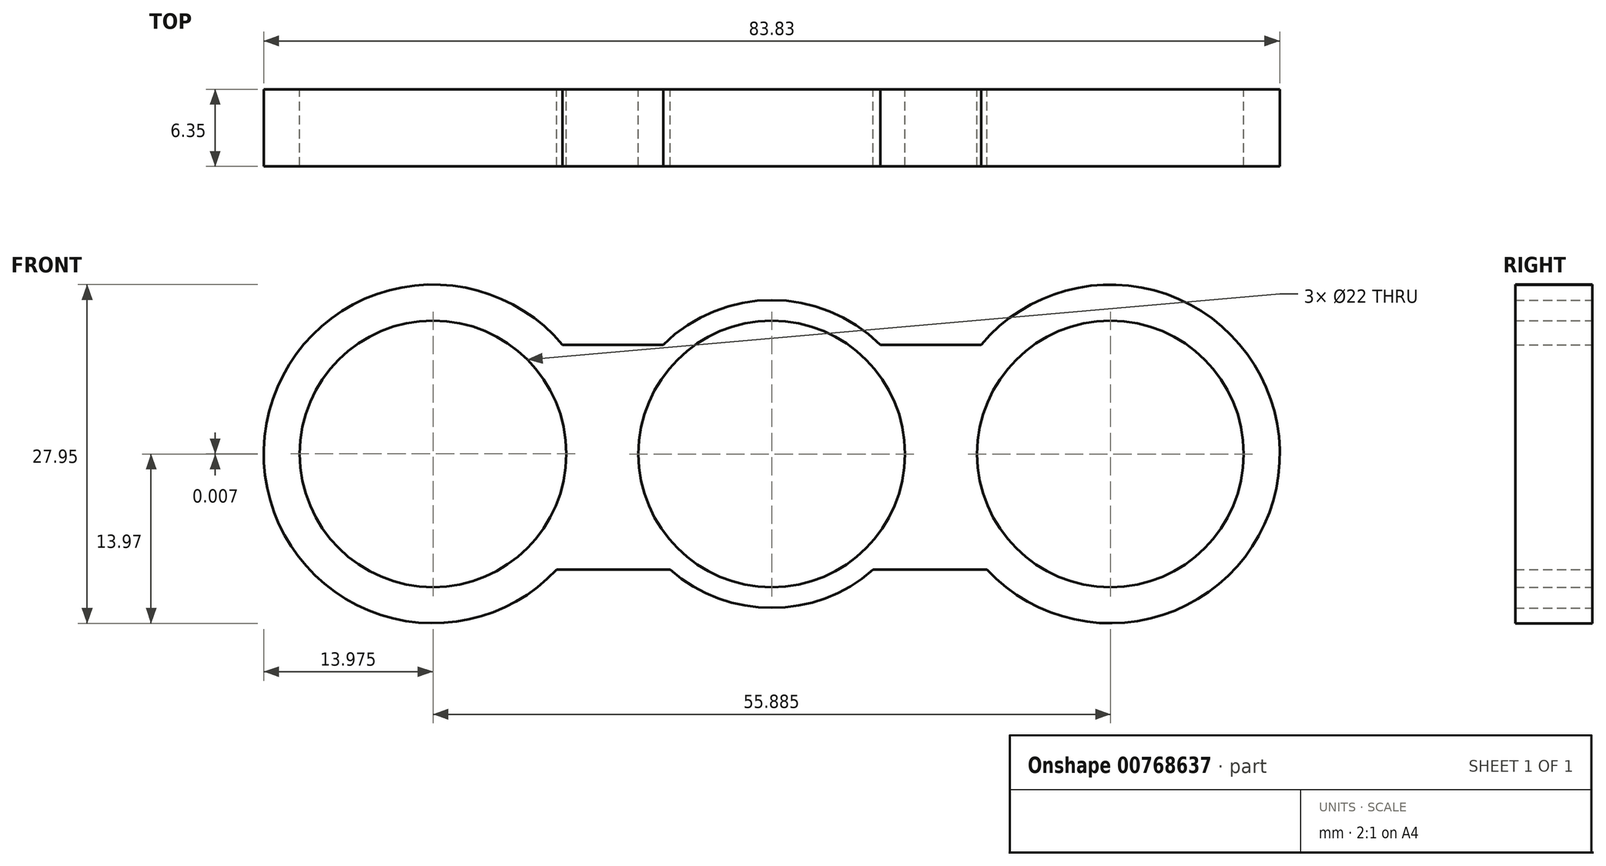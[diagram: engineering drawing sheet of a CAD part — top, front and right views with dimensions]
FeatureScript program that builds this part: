
annotation { "Feature Type Name" : "Feature", "Feature Type Description" : "" }
export const myFeature = defineFeature(function(context is Context, id is Id, definition is map)
    precondition{}
    {
        {
            var Q0;
            Q0=qCreatedBy(makeId("Front.planeOp"),FACE);
            var sketch = newSketch(context, id + "F0", { "sketchPlane" : qUnion([Q0])});
            skCircle(sketch, "E0", {"center": v(0, 0) * mm, "radius": 11 * mm});
            skCircle(sketch, "E1", {"center": v(27.94, 0) * mm, "radius": 11 * mm});
            skCircle(sketch, "E2", {"center": v(-27.95, 0) * mm, "radius": 11 * mm});
            skCircle(sketch, "E3", {"center": v(-27.95, 0) * mm, "radius": 13.97 * mm});
            skCircle(sketch, "E4", {"center": v(27.94, 0) * mm, "radius": 13.97 * mm});
            skCircle(sketch, "E5", {"center": v(0, 0) * mm, "radius": 12.7 * mm});
            skLineSegment(sketch, "E6", {"start": v(-17.27, 9.02) * mm, "end": v(-8.94, 9.02) * mm});
            skLineSegment(sketch, "E7", {"start": v(8.94, 9.02) * mm, "end": v(17.27, 9.02) * mm});
            skLineSegment(sketch, "E8", {"start": v(-17.76, -9.55) * mm, "end": v(-8.37, -9.55) * mm});
            skLineSegment(sketch, "E9", {"start": v(8.37, -9.55) * mm, "end": v(17.75, -9.55) * mm});
            skSolve(sketch);
        }
        {
            var Q0;
            Q0 = qSketchRegion(id + "F0", true);
            extrude(context, id + "F1", {"entities" : qUnion([Q0]), "depth" : 6.35 * mm, "offsetDistance" : 25.4 * mm});
        }
    });
